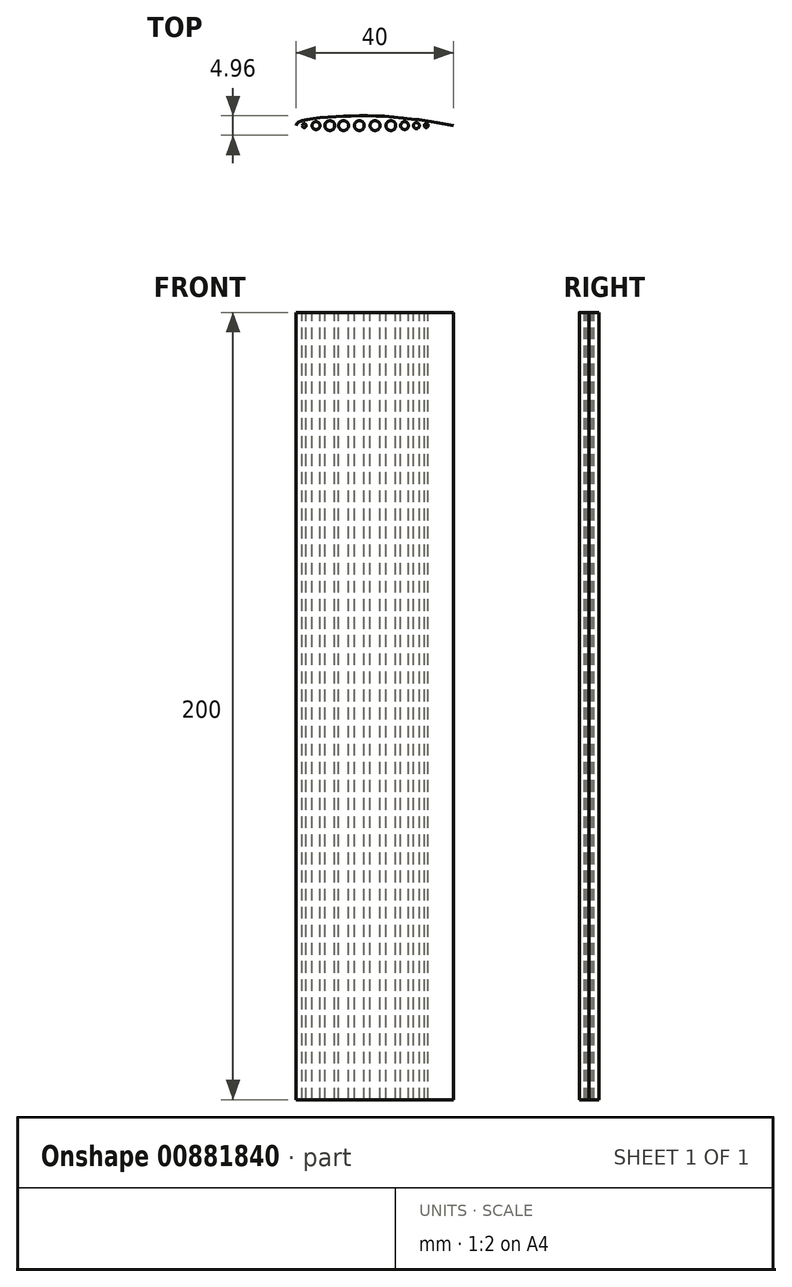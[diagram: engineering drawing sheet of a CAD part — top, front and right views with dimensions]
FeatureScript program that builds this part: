
annotation { "Feature Type Name" : "Feature", "Feature Type Description" : "" }
export const myFeature = defineFeature(function(context is Context, id is Id, definition is map)
    precondition{}
    {
        {
            var Q0;
            Q0=qCreatedBy(makeId("Top.planeOp"),FACE);
            var sketch = newSketch(context, id + "F0", { "sketchPlane" : qUnion([Q0])});
            skFitSpline(sketch, "E0", {"points": [v(-20.08, 0) * mm, v(-19.7, 0.74) * mm, v(-18.07, 1.4) * mm, v(-15.64, 1.83) * mm, v(-11.3, 2.2) * mm, v(-7.07, 2.42) * mm, v(-2.09, 2.48) * mm, v(3.23, 2.3) * mm, v(9.35, 1.67) * mm, v(12.6, 1.29) * mm, v(15.31, 0.85) * mm, v(17.59, 0.47) * mm, v(19.92, 0) * mm], "startDerivative": vector(6.31, 19.65) * mm, "endDerivative": vector(32.77, -6.96) * mm});
            skLineSegment(sketch, "E1", {"start": v(-20.08, 0) * mm, "end": v(19.92, 0) * mm, "construction": true});
            skFitSpline(sketch, "E2.MirrorCS", {"points": [v(-20.08, 0) * mm, v(-19.7, -0.74) * mm, v(-18.07, -1.4) * mm, v(-15.64, -1.83) * mm, v(-11.3, -2.2) * mm, v(-7.07, -2.42) * mm, v(-2.09, -2.48) * mm, v(3.23, -2.3) * mm, v(9.35, -1.67) * mm, v(12.6, -1.29) * mm, v(15.31, -0.85) * mm, v(17.59, -0.47) * mm, v(19.92, 0) * mm], "startDerivative": vector(6.31, -19.65) * mm, "endDerivative": vector(32.77, 6.96) * mm});
            skCircle(sketch, "E3", {"center": v(0, 0) * mm, "radius": 1.25 * mm});
            skCircle(sketch, "E4", {"center": v(-18, 0) * mm, "radius": 0.5 * mm});
            skCircle(sketch, "E5", {"center": v(-15, 0) * mm, "radius": 1 * mm});
            skCircle(sketch, "E6", {"center": v(-8, 0) * mm, "radius": 1.25 * mm});
            skCircle(sketch, "E7", {"center": v(-4, 0) * mm, "radius": 1.25 * mm});
            skCircle(sketch, "E8", {"center": v(-11.5, 0) * mm, "radius": 1.25 * mm});
            skCircle(sketch, "E9", {"center": v(4, 0) * mm, "radius": 1.25 * mm});
            skCircle(sketch, "E10", {"center": v(7.5, 0) * mm, "radius": 1 * mm});
            skCircle(sketch, "E11", {"center": v(10.5, 0) * mm, "radius": 0.75 * mm});
            skCircle(sketch, "E12", {"center": v(13, 0) * mm, "radius": 0.5 * mm});
            skSolve(sketch);
        }
        {
            var Q0;
            Q0=sQuery(id+"F0.wireOp",EDGE,"E0");
            var Q1;
            Q1=sQuery(id+"F0.wireOp",EDGE,"E2.MirrorCS");
            var Q2;
            Q2=sQuery(id+"F0.wireOp",EDGE,"E4");
            var Q3;
            Q3=sQuery(id+"F0.wireOp",EDGE,"E5");
            var Q4;
            Q4=sQuery(id+"F0.wireOp",EDGE,"E8");
            var Q5;
            Q5=sQuery(id+"F0.wireOp",EDGE,"E6");
            var Q6;
            Q6=sQuery(id+"F0.wireOp",EDGE,"E7");
            var Q7;
            Q7=sQuery(id+"F0.wireOp",EDGE,"E3");
            var Q8;
            Q8=sQuery(id+"F0.wireOp",EDGE,"E9");
            var Q9;
            Q9=sQuery(id+"F0.wireOp",EDGE,"E10");
            var Q10;
            Q10=sQuery(id+"F0.wireOp",EDGE,"E12");
            var Q11;
            Q11=sQuery(id+"F0.wireOp",EDGE,"jUKZs80J-ieqI-r39s-LPQ2-U2W05SsCXCWb");
            var Q12;
            Q12=sQuery(id+"F0.wireOp",EDGE,"E11");
            extrude(context, id + "F1", {"bodyType" : ToolBodyType.SURFACE, "surfaceEntities" : qUnion([Q0, Q1, Q2, Q3, Q4, Q5, Q6, Q7, Q8, Q9, Q10, Q11, Q12]), "depth" : 200 * mm, "offsetDistance" : 25 * mm});
        }
    });
